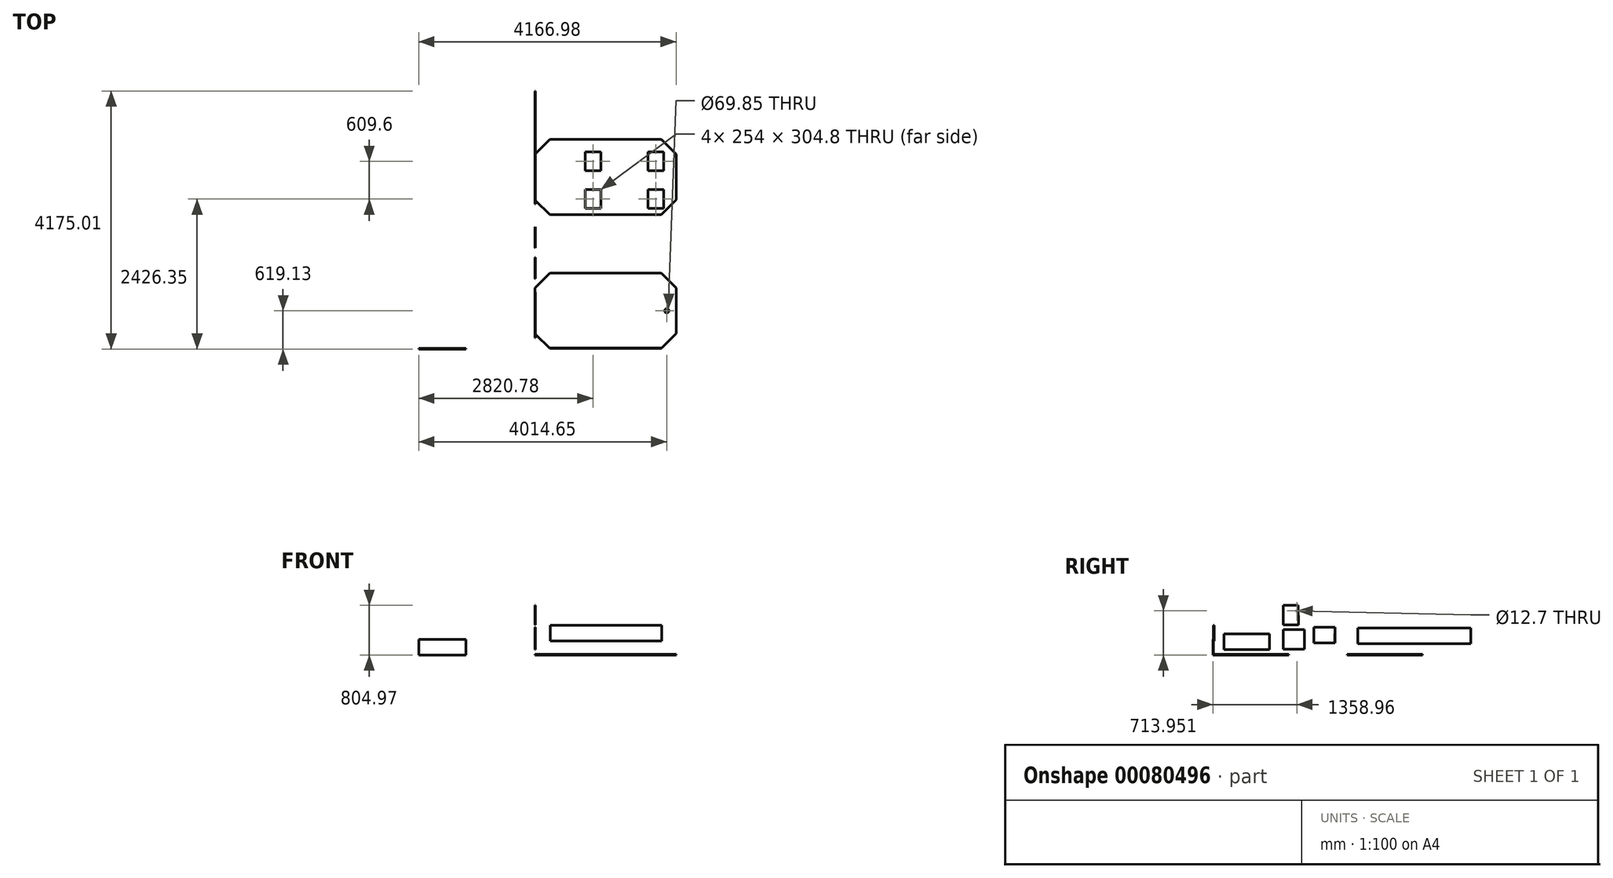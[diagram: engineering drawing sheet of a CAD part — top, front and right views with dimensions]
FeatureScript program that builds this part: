
annotation { "Feature Type Name" : "Feature", "Feature Type Description" : "" }
export const myFeature = defineFeature(function(context is Context, id is Id, definition is map)
    precondition{}
    {
        {
            var Q0;
            Q0=qCreatedBy(makeId("Top.planeOp"),FACE);
            var sketch = newSketch(context, id + "F0", { "sketchPlane" : qUnion([Q0])});
            skLineSegment(sketch, "E0.bottom", {"start": v(0, 0) * mm, "end": v(2438.4, 0) * mm});
            skLineSegment(sketch, "E0.top", {"start": v(0, 1219.2) * mm, "end": v(2438.4, 1219.2) * mm});
            skLineSegment(sketch, "E0.left", {"start": v(0, 0) * mm, "end": v(0, 1219.2) * mm});
            skLineSegment(sketch, "E0.right", {"start": v(2438.4, 0) * mm, "end": v(2438.4, 1219.2) * mm});
            skSolve(sketch);
        }
        {
            var Q0;
            Q0=makeQuery(id+"F0.imprint","IMPRINT",FACE,{"disambiguationData":[TD([[makeQuery(id+"F0.imprint","IMPRINT",EDGE,{"derivedFrom":sQuery(id+"F0.wireOp",EDGE,"E0.bottom")}),1.0]])]});
            extrude(context, id + "F1", {"entities" : qUnion([Q0]), "depth" : 9.52 * mm});
        }
        {
            var Q0;
            Q0=makeQuery(id+"F1.opExtrude","CAP_FACE",FACE,{"disambiguationData":[OSD([sQuery(id+"F0.wireOp",EDGE,"E0.bottom"),sQuery(id+"F0.wireOp",EDGE,"E0.top"),sQuery(id+"F0.wireOp",EDGE,"E0.left"),sQuery(id+"F0.wireOp",EDGE,"E0.right")])],"isStart":false});
            var sketch = newSketch(context, id + "F2", { "sketchPlane" : qUnion([Q0])});
            skLineSegment(sketch, "E1", {"start": v(0, 977.9) * mm, "end": v(241.3, 1219.2) * mm});
            skLineSegment(sketch, "E2", {"start": v(241.3, 1219.2) * mm, "end": v(0, 1219.2) * mm});
            skLineSegment(sketch, "E3", {"start": v(0, 1219.2) * mm, "end": v(0, 977.9) * mm});
            skLineSegment(sketch, "E4", {"start": v(0, 241.3) * mm, "end": v(241.3, 0) * mm});
            skLineSegment(sketch, "E5", {"start": v(241.3, 0) * mm, "end": v(0, 0) * mm});
            skLineSegment(sketch, "E6", {"start": v(0, 0) * mm, "end": v(0, 241.3) * mm});
            skSolve(sketch);
        }
        {
            var Q0;
            Q0=makeQuery(id+"F2.imprint","IMPRINT",FACE,{"disambiguationData":[TD([[makeQuery(id+"F2.imprint","IMPRINT",EDGE,{"derivedFrom":sQuery(id+"F2.wireOp",EDGE,"E1")}),1.0]])]});
            var Q1;
            Q1=makeQuery(id+"F2.imprint","IMPRINT",FACE,{"disambiguationData":[TD([[makeQuery(id+"F2.imprint","IMPRINT",EDGE,{"derivedFrom":sQuery(id+"F2.wireOp",EDGE,"E4")}),-1.0]])]});
            extrude(context, id + "F3", {"entities" : qUnion([Q0, Q1]), "operationType" : NewBodyOperationType.REMOVE, "oppositeDirection" : true, "depth" : 25.4 * mm});
        }
        {
            var Q0;
            Q0=makeQuery(id+"F1.opExtrude","CAP_FACE",FACE,{"disambiguationData":[OSD([sQuery(id+"F0.wireOp",EDGE,"E0.bottom"),sQuery(id+"F0.wireOp",EDGE,"E0.top"),sQuery(id+"F0.wireOp",EDGE,"E0.left"),sQuery(id+"F0.wireOp",EDGE,"E0.right")])],"isStart":false});
            var sketch = newSketch(context, id + "F4", { "sketchPlane" : qUnion([Q0])});
            skLineSegment(sketch, "E7.bottom", {"start": v(2438.4, 1219.2) * mm, "end": v(2044.7, 1219.2) * mm});
            skLineSegment(sketch, "E7.top", {"start": v(2438.4, 0) * mm, "end": v(2044.7, 0) * mm});
            skLineSegment(sketch, "E7.left", {"start": v(2438.4, 1219.2) * mm, "end": v(2438.4, 0) * mm});
            skLineSegment(sketch, "E8", {"start": v(2044.7, 1219.2) * mm, "end": v(2286, 977.9) * mm});
            skLineSegment(sketch, "E9", {"start": v(2286, 977.9) * mm, "end": v(2286, 241.3) * mm});
            skLineSegment(sketch, "E10", {"start": v(2286, 241.3) * mm, "end": v(2044.7, 0) * mm});
            skSolve(sketch);
        }
        {
            var Q0;
            Q0=makeQuery(id+"F4.imprint","IMPRINT",FACE,{"disambiguationData":[TD([[makeQuery(id+"F4.imprint","IMPRINT",EDGE,{"derivedFrom":sQuery(id+"F4.wireOp",EDGE,"E7.bottom")}),-1.0]])]});
            extrude(context, id + "F5", {"entities" : qUnion([Q0]), "operationType" : NewBodyOperationType.REMOVE, "oppositeDirection" : true, "depth" : 25.4 * mm});
        }
        {
            var Q0;
            Q0=qCreatedBy(makeId("Right.planeOp"),FACE);
            var sketch = newSketch(context, id + "F6", { "sketchPlane" : qUnion([Q0])});
            skLineSegment(sketch, "E11.bottom", {"start": v(172.56, 90.85) * mm, "end": v(909.16, 90.85) * mm});
            skLineSegment(sketch, "E11.top", {"start": v(172.56, 344.85) * mm, "end": v(909.16, 344.85) * mm});
            skLineSegment(sketch, "E11.left", {"start": v(172.56, 90.85) * mm, "end": v(172.56, 344.85) * mm});
            skLineSegment(sketch, "E11.right", {"start": v(909.16, 90.85) * mm, "end": v(909.16, 344.85) * mm});
            skSolve(sketch);
        }
        {
            var Q0;
            Q0=makeQuery(id+"F6.imprint","IMPRINT",FACE,{"disambiguationData":[TD([[makeQuery(id+"F6.imprint","IMPRINT",EDGE,{"derivedFrom":sQuery(id+"F6.wireOp",EDGE,"E11.bottom")}),1.0]])]});
            extrude(context, id + "F7", {"entities" : qUnion([Q0]), "depth" : 9.52 * mm});
        }
        {
            var Q0;
            Q0=qCreatedBy(makeId("Front.planeOp"),FACE);
            var sketch = newSketch(context, id + "F8", { "sketchPlane" : qUnion([Q0])});
            skLineSegment(sketch, "E12.top", {"start": v(2054.27, 480.87) * mm, "end": v(250.87, 480.87) * mm});
            skLineSegment(sketch, "E12.left", {"start": v(2054.27, 226.87) * mm, "end": v(2054.27, 480.87) * mm});
            skLineSegment(sketch, "E12.right", {"start": v(250.87, 226.87) * mm, "end": v(250.87, 480.87) * mm});
            skLineSegment(sketch, "E13", {"start": v(250.87, 226.87) * mm, "end": v(2054.27, 226.87) * mm});
            skSolve(sketch);
        }
        {
            var Q0;
            Q0=makeQuery(id+"F8.imprint","IMPRINT",FACE,{"disambiguationData":[TD([[makeQuery(id+"F8.imprint","IMPRINT",EDGE,{"derivedFrom":sQuery(id+"F8.wireOp",EDGE,"E12.bottom")}),-1.0]])]});
            var Q1;
            Q1=makeQuery(id+"F8.imprint","IMPRINT",FACE,{"disambiguationData":[TD([[makeQuery(id+"F8.imprint","IMPRINT",EDGE,{"derivedFrom":sQuery(id+"F8.wireOp",EDGE,"E12.top")}),1.0]])]});
            extrude(context, id + "F9", {"entities" : qUnion([Q0, Q1]), "oppositeDirection" : true, "depth" : 9.52 * mm});
        }
        {
            var Q0;
            Q0=qCreatedBy(makeId("Right.planeOp"),FACE);
            var sketch = newSketch(context, id + "F10", { "sketchPlane" : qUnion([Q0])});
            skLineSegment(sketch, "E14.bottom", {"start": v(28.65, 498.38) * mm, "end": v(765.25, 498.38) * mm});
            skLineSegment(sketch, "E14.top", {"start": v(28.65, 815.88) * mm, "end": v(765.25, 815.88) * mm});
            skLineSegment(sketch, "E14.left", {"start": v(28.65, 498.38) * mm, "end": v(28.65, 815.88) * mm});
            skLineSegment(sketch, "E14.right", {"start": v(765.25, 498.38) * mm, "end": v(765.25, 815.88) * mm});
            skSolve(sketch);
        }
        {
            var Q0;
            Q0=makeQuery(id+"F10.imprint","IMPRINT",FACE,{"disambiguationData":[TD([[makeQuery(id+"F10.imprint","IMPRINT",EDGE,{"derivedFrom":sQuery(id+"F10.wireOp",EDGE,"E14.bottom")}),1.0]])]});
            extrude(context, id + "F11", {"entities" : qUnion([Q0]), "depth" : 9.52 * mm});
        }
        {
            var Q0;
            Q0=qCreatedBy(makeId("Right.planeOp"),FACE);
            var sketch = newSketch(context, id + "F12", { "sketchPlane" : qUnion([Q0])});
            skLineSegment(sketch, "E15.bottom", {"start": v(1130.12, 487.47) * mm, "end": v(1384.12, 487.47) * mm});
            skLineSegment(sketch, "E15.top", {"start": v(1130.12, 804.97) * mm, "end": v(1384.12, 804.97) * mm});
            skLineSegment(sketch, "E15.left", {"start": v(1130.12, 487.47) * mm, "end": v(1130.12, 804.97) * mm});
            skLineSegment(sketch, "E15.right", {"start": v(1384.12, 487.47) * mm, "end": v(1384.12, 804.97) * mm});
            skSolve(sketch);
        }
        {
            var Q0;
            Q0=makeQuery(id+"F12.imprint","IMPRINT",FACE,{"disambiguationData":[TD([[makeQuery(id+"F12.imprint","IMPRINT",EDGE,{"derivedFrom":sQuery(id+"F12.wireOp",EDGE,"E15.bottom")}),1.0]])]});
            extrude(context, id + "F13", {"entities" : qUnion([Q0]), "depth" : 9.52 * mm});
        }
        {
            var Q0;
            Q0=makeQuery(id+"F13.opExtrude","SWEPT_FACE",FACE,{"disambiguationData":[OSD([sQuery(id+"F12.wireOp",EDGE,"E15.top")])]});
            var sketch = newSketch(context, id + "F14", { "sketchPlane" : qUnion([Q0])});
            skLineSegment(sketch, "E16", {"start": v(9.53, 1130.12) * mm, "end": v(0, 1139.64) * mm});
            skLineSegment(sketch, "E17", {"start": v(0, 1139.64) * mm, "end": v(0, 1130.12) * mm});
            skLineSegment(sketch, "E18", {"start": v(0, 1130.12) * mm, "end": v(9.52, 1130.12) * mm});
            skSolve(sketch);
        }
        {
            var Q0;
            Q0=makeQuery(id+"F14.imprint","IMPRINT",FACE,{"disambiguationData":[TD([[makeQuery(id+"F14.imprint","IMPRINT",EDGE,{"derivedFrom":sQuery(id+"F14.wireOp",EDGE,"i4C3c2Mx-m0kE-4Q8j-UAPY-lbmBrqHYXmZ3")}),-1.0]])]});
            var Q1;
            Q1=makeQuery(id+"F14.imprint","IMPRINT",FACE,{"disambiguationData":[TD([[makeQuery(id+"F14.imprint","IMPRINT",EDGE,{"derivedFrom":sQuery(id+"F14.wireOp",EDGE,"E16")}),1.0]])]});
            extrude(context, id + "F15", {"entities" : qUnion([Q0, Q1]), "operationType" : NewBodyOperationType.REMOVE, "oppositeDirection" : true, "depth" : 317.5 * mm});
        }
        {
            var Q0;
            Q0=makeQuery(id+"F13.opExtrude","SWEPT_EDGE",EDGE,{"disambiguationData":[OSD([sQuery(id+"F12.wireOp",EDGE,"E15.bottom"),sQuery(id+"F12.wireOp",EDGE,"E15.right")])]});
            var Q1;
            Q1=makeQuery(id+"F13.opExtrude","CAP_EDGE",EDGE,{"disambiguationData":[OSD([sQuery(id+"F12.wireOp",EDGE,"E15.bottom")])],"isStart":false});
            cPlane(context, id + "F16", {"entities" : qUnion([Q0, Q1]), "cplaneType" : CPlaneType.LINE_ANGLE, "offset" : 152.4 * mm, "angle" : 358.3 * degree, "width" : 152.4 * mm, "height" : 152.4 * mm});
        }
        {
            var Q0;
            Q0=qCreatedBy(id+"F16.planeOp",FACE);
            var sketch = newSketch(context, id + "F17", { "sketchPlane" : qUnion([Q0])});
            skLineSegment(sketch, "E19", {"start": v(9.54, -1393.98) * mm, "end": v(0, -1384.94) * mm});
            skLineSegment(sketch, "E20", {"start": v(0, -1384.94) * mm, "end": v(0, -1420.44) * mm});
            skLineSegment(sketch, "E21", {"start": v(0, -1420.44) * mm, "end": v(10.09, -1420.44) * mm});
            skLineSegment(sketch, "E22", {"start": v(10.09, -1420.44) * mm, "end": v(10.09, -1394.5) * mm});
            skLineSegment(sketch, "E23", {"start": v(9.54, -1393.98) * mm, "end": v(10.09, -1394.5) * mm});
            skSolve(sketch);
        }
        {
            var Q0;
            Q0=makeQuery(id+"F17.imprint","IMPRINT",FACE,{"disambiguationData":[TD([[makeQuery(id+"F17.imprint","IMPRINT",EDGE,{"derivedFrom":sQuery(id+"F17.wireOp",EDGE,"E19")}),1.0]])]});
            extrude(context, id + "F18", {"entities" : qUnion([Q0]), "operationType" : NewBodyOperationType.REMOVE, "oppositeDirection" : true, "depth" : 330.2 * mm});
        }
        {
            var Q0;
            Q0=makeQuery(id+"F13.opExtrude","CAP_FACE",FACE,{"disambiguationData":[OSD([sQuery(id+"F12.wireOp",EDGE,"E15.bottom"),sQuery(id+"F12.wireOp",EDGE,"E15.top"),sQuery(id+"F12.wireOp",EDGE,"E15.left"),sQuery(id+"F12.wireOp",EDGE,"E15.right")])],"isStart":false});
            var sketch = newSketch(context, id + "F19", { "sketchPlane" : qUnion([Q0])});
            skCircle(sketch, "E24", {"center": v(1349.43, 713.95) * mm, "radius": 6.35 * mm});
            skSolve(sketch);
        }
        {
            var Q0;
            Q0=makeQuery(id+"F19.imprint","IMPRINT",FACE,{"disambiguationData":[TD([[makeQuery(id+"F19.imprint","IMPRINT",EDGE,{"derivedFrom":sQuery(id+"F19.wireOp",EDGE,"E24")}),1.0]])]});
            extrude(context, id + "F20", {"entities" : qUnion([Q0]), "operationType" : NewBodyOperationType.REMOVE, "oppositeDirection" : true, "depth" : 25.4 * mm});
        }
        {
            var Q0;
            Q0=qCreatedBy(makeId("Right.planeOp"),FACE);
            var sketch = newSketch(context, id + "F21", { "sketchPlane" : qUnion([Q0])});
            skLineSegment(sketch, "E25.bottom", {"start": v(1131.07, 411.37) * mm, "end": v(1473.97, 411.37) * mm});
            skLineSegment(sketch, "E25.top", {"start": v(1131.07, 93.87) * mm, "end": v(1473.97, 93.87) * mm});
            skLineSegment(sketch, "E25.left", {"start": v(1131.07, 411.37) * mm, "end": v(1131.07, 93.87) * mm});
            skLineSegment(sketch, "E25.right", {"start": v(1473.97, 411.37) * mm, "end": v(1473.97, 93.87) * mm});
            skSolve(sketch);
        }
        {
            var Q0;
            Q0=qCreatedBy(makeId("Right.planeOp"),FACE);
            var sketch = newSketch(context, id + "F22", { "sketchPlane" : qUnion([Q0])});
            skLineSegment(sketch, "E26.bottom", {"start": v(1623.64, 450.22) * mm, "end": v(1966.54, 450.22) * mm});
            skLineSegment(sketch, "E26.top", {"start": v(1623.64, 196.22) * mm, "end": v(1966.54, 196.22) * mm});
            skLineSegment(sketch, "E26.left", {"start": v(1623.64, 450.22) * mm, "end": v(1623.64, 196.22) * mm});
            skLineSegment(sketch, "E26.right", {"start": v(1966.54, 450.22) * mm, "end": v(1966.54, 196.22) * mm});
            skSolve(sketch);
        }
        {
            var Q0;
            Q0=makeQuery(id+"F21.imprint","IMPRINT",FACE,{"disambiguationData":[TD([[makeQuery(id+"F21.imprint","IMPRINT",EDGE,{"derivedFrom":sQuery(id+"F21.wireOp",EDGE,"E25.bottom")}),-1.0]])]});
            extrude(context, id + "F23", {"entities" : qUnion([Q0]), "depth" : 9.52 * mm});
        }
        {
            var Q0;
            Q0=makeQuery(id+"F22.imprint","IMPRINT",FACE,{"disambiguationData":[TD([[makeQuery(id+"F22.imprint","IMPRINT",EDGE,{"derivedFrom":sQuery(id+"F22.wireOp",EDGE,"E26.bottom")}),-1.0]])]});
            extrude(context, id + "F24", {"entities" : qUnion([Q0]), "depth" : 9.52 * mm});
        }
        {
            var Q0;
            Q0=qCreatedBy(makeId("Top.planeOp"),FACE);
            var sketch = newSketch(context, id + "F25", { "sketchPlane" : qUnion([Q0])});
            skLineSegment(sketch, "E27.bottom", {"start": v(0, 2162.82) * mm, "end": v(2286, 2162.82) * mm});
            skLineSegment(sketch, "E27.top", {"start": v(0, 3382.02) * mm, "end": v(2286, 3382.02) * mm});
            skLineSegment(sketch, "E27.left", {"start": v(0, 2162.82) * mm, "end": v(0, 3382.02) * mm});
            skLineSegment(sketch, "E27.right", {"start": v(2286, 2162.82) * mm, "end": v(2286, 3382.02) * mm});
            skSolve(sketch);
        }
        {
            var Q0;
            Q0=makeQuery(id+"F25.imprint","IMPRINT",FACE,{"disambiguationData":[TD([[makeQuery(id+"F25.imprint","IMPRINT",EDGE,{"derivedFrom":sQuery(id+"F25.wireOp",EDGE,"E27.bottom")}),1.0]])]});
            extrude(context, id + "F26", {"entities" : qUnion([Q0]), "depth" : 9.52 * mm});
        }
        {
            var Q0;
            Q0=makeQuery(id+"F26.opExtrude","CAP_FACE",FACE,{"disambiguationData":[OSD([sQuery(id+"F25.wireOp",EDGE,"E27.bottom"),sQuery(id+"F25.wireOp",EDGE,"E27.top"),sQuery(id+"F25.wireOp",EDGE,"E27.left"),sQuery(id+"F25.wireOp",EDGE,"E27.right")])],"isStart":false});
            var sketch = newSketch(context, id + "F27", { "sketchPlane" : qUnion([Q0])});
            skLineSegment(sketch, "E28.bottom", {"start": v(0, 3382.02) * mm, "end": v(241.3, 3382.02) * mm});
            skLineSegment(sketch, "E28.left", {"start": v(0, 3382.02) * mm, "end": v(0, 3140.72) * mm});
            skLineSegment(sketch, "E29.bottom", {"start": v(0, 2162.82) * mm, "end": v(241.3, 2162.82) * mm});
            skLineSegment(sketch, "E29.left", {"start": v(0, 2162.82) * mm, "end": v(0, 2404.12) * mm});
            skLineSegment(sketch, "E30.bottom", {"start": v(2286, 3382.02) * mm, "end": v(2044.7, 3382.02) * mm});
            skLineSegment(sketch, "E31.bottom", {"start": v(2286, 2162.82) * mm, "end": v(2044.7, 2162.82) * mm});
            skLineSegment(sketch, "E32", {"start": v(0, 3140.72) * mm, "end": v(241.3, 3382.02) * mm});
            skLineSegment(sketch, "E33", {"start": v(0, 2404.12) * mm, "end": v(241.3, 2162.82) * mm});
            skLineSegment(sketch, "E34", {"start": v(2286, 3382.02) * mm, "end": v(2286, 3140.72) * mm});
            skLineSegment(sketch, "E35", {"start": v(2286, 3140.72) * mm, "end": v(2044.7, 3382.02) * mm});
            skLineSegment(sketch, "E36", {"start": v(2286, 2162.82) * mm, "end": v(2286, 2404.12) * mm});
            skLineSegment(sketch, "E37", {"start": v(2286, 2404.12) * mm, "end": v(2044.7, 2162.82) * mm});
            skSolve(sketch);
        }
        {
            var Q0;
            Q0=makeQuery(id+"F27.imprint","IMPRINT",FACE,{"disambiguationData":[TD([[makeQuery(id+"F27.imprint","IMPRINT",EDGE,{"derivedFrom":sQuery(id+"F27.wireOp",EDGE,"E28.bottom")}),-1.0]])]});
            var Q1;
            Q1=makeQuery(id+"F27.imprint","IMPRINT",FACE,{"disambiguationData":[TD([[makeQuery(id+"F27.imprint","IMPRINT",EDGE,{"derivedFrom":sQuery(id+"F27.wireOp",EDGE,"E29.bottom")}),1.0]])]});
            var Q2;
            Q2=makeQuery(id+"F27.imprint","IMPRINT",FACE,{"disambiguationData":[TD([[makeQuery(id+"F27.imprint","IMPRINT",EDGE,{"derivedFrom":sQuery(id+"F27.wireOp",EDGE,"E30.bottom")}),-1.0]])]});
            var Q3;
            Q3=makeQuery(id+"F27.imprint","IMPRINT",FACE,{"disambiguationData":[TD([[makeQuery(id+"F27.imprint","IMPRINT",EDGE,{"derivedFrom":sQuery(id+"F27.wireOp",EDGE,"E31.bottom")}),1.0]])]});
            extrude(context, id + "F28", {"entities" : qUnion([Q0, Q1, Q2, Q3]), "operationType" : NewBodyOperationType.REMOVE, "oppositeDirection" : true, "depth" : 25.4 * mm});
        }
        {
            var Q0;
            Q0=makeQuery(id+"F1.opExtrude","CAP_EDGE",EDGE,{"disambiguationData":[OSD([sQuery(id+"F0.wireOp",EDGE,"E0.left")])],"isStart":false});
            cPlane(context, id + "F29", {"entities" : qUnion([Q0]), "cplaneType" : CPlaneType.LINE_ANGLE, "offset" : 152.4 * mm, "angle" : 358.8 * degree, "width" : 152.4 * mm, "height" : 152.4 * mm});
        }
        {
            var Q0;
            Q0=qCreatedBy(id+"F29.planeOp",FACE);
            var sketch = newSketch(context, id + "F30", { "sketchPlane" : qUnion([Q0])});
            skLineSegment(sketch, "E38.bottom", {"start": v(0, 211.48) * mm, "end": v(-33.38, 211.48) * mm});
            skLineSegment(sketch, "E38.top", {"start": v(0, 1019.73) * mm, "end": v(-33.38, 1019.73) * mm});
            skLineSegment(sketch, "E38.left", {"start": v(0, 211.48) * mm, "end": v(0, 1019.73) * mm});
            skLineSegment(sketch, "E38.right", {"start": v(-33.38, 211.48) * mm, "end": v(-33.38, 1019.73) * mm});
            skSolve(sketch);
        }
        {
            var Q0;
            Q0=makeQuery(id+"F30.imprint","IMPRINT",FACE,{"disambiguationData":[TD([[makeQuery(id+"F30.imprint","IMPRINT",EDGE,{"derivedFrom":sQuery(id+"F30.wireOp",EDGE,"E38.bottom")}),-1.0]])]});
            extrude(context, id + "F31", {"entities" : qUnion([Q0]), "operationType" : NewBodyOperationType.REMOVE, "oppositeDirection" : true, "depth" : 25.4 * mm});
        }
        {
            var Q0;
            Q0=qCreatedBy(makeId("Right.planeOp"),FACE);
            var sketch = newSketch(context, id + "F32", { "sketchPlane" : qUnion([Q0])});
            skLineSegment(sketch, "E39.bottom", {"start": v(2336.68, 182.8) * mm, "end": v(4165.48, 182.8) * mm});
            skLineSegment(sketch, "E39.top", {"start": v(2336.68, 436.8) * mm, "end": v(4165.48, 436.8) * mm});
            skLineSegment(sketch, "E39.left", {"start": v(2336.68, 182.8) * mm, "end": v(2336.68, 436.8) * mm});
            skLineSegment(sketch, "E39.right", {"start": v(4165.48, 182.8) * mm, "end": v(4165.48, 436.8) * mm});
            skSolve(sketch);
        }
        {
            var Q0;
            Q0=makeQuery(id+"F32.imprint","IMPRINT",FACE,{"disambiguationData":[TD([[makeQuery(id+"F32.imprint","IMPRINT",EDGE,{"derivedFrom":sQuery(id+"F32.wireOp",EDGE,"E39.bottom")}),1.0]])]});
            extrude(context, id + "F33", {"entities" : qUnion([Q0]), "depth" : 9.52 * mm});
        }
        {
            var Q0;
            Q0=qCreatedBy(makeId("Front.planeOp"),FACE);
            var sketch = newSketch(context, id + "F34", { "sketchPlane" : qUnion([Q0])});
            skLineSegment(sketch, "E40.bottom", {"start": v(-1118.98, 0) * mm, "end": v(-1880.98, 0) * mm});
            skLineSegment(sketch, "E40.top", {"start": v(-1118.98, 254) * mm, "end": v(-1880.98, 254) * mm});
            skLineSegment(sketch, "E40.left", {"start": v(-1118.98, 0) * mm, "end": v(-1118.98, 254) * mm});
            skLineSegment(sketch, "E40.right", {"start": v(-1880.98, 0) * mm, "end": v(-1880.98, 254) * mm});
            skSolve(sketch);
        }
        {
            var Q0;
            Q0=makeQuery(id+"F34.imprint","IMPRINT",FACE,{"disambiguationData":[TD([[makeQuery(id+"F34.imprint","IMPRINT",EDGE,{"derivedFrom":sQuery(id+"F34.wireOp",EDGE,"E40.bottom")}),-1.0]])]});
            extrude(context, id + "F35", {"entities" : qUnion([Q0]), "depth" : 9.52 * mm});
        }
        {
            var Q0;
            Q0=makeQuery(id+"F24.opExtrude","SWEPT_FACE",FACE,{"disambiguationData":[OSD([sQuery(id+"F22.wireOp",EDGE,"E26.bottom")])]});
            var sketch = newSketch(context, id + "F36", { "sketchPlane" : qUnion([Q0])});
            skLineSegment(sketch, "E41", {"start": v(9.53, 1966.54) * mm, "end": v(0, 1957.02) * mm});
            skLineSegment(sketch, "E42", {"start": v(0, 1957.02) * mm, "end": v(0, 1966.54) * mm});
            skLineSegment(sketch, "E43", {"start": v(0, 1966.54) * mm, "end": v(9.52, 1966.54) * mm});
            skLineSegment(sketch, "E44", {"start": v(0, 1623.64) * mm, "end": v(0, 1633.17) * mm});
            skLineSegment(sketch, "E45", {"start": v(0, 1633.17) * mm, "end": v(9.52, 1623.64) * mm});
            skLineSegment(sketch, "E46", {"start": v(9.52, 1623.64) * mm, "end": v(0, 1623.64) * mm});
            skSolve(sketch);
        }
        {
            var Q0;
            Q0=makeQuery(id+"F36.imprint","IMPRINT",FACE,{"disambiguationData":[TD([[makeQuery(id+"F36.imprint","IMPRINT",EDGE,{"derivedFrom":sQuery(id+"F36.wireOp",EDGE,"E41")}),-1.0]])]});
            var Q1;
            Q1=makeQuery(id+"F36.imprint","IMPRINT",FACE,{"disambiguationData":[TD([[makeQuery(id+"F36.imprint","IMPRINT",EDGE,{"derivedFrom":sQuery(id+"F36.wireOp",EDGE,"E44")}),-1.0]])]});
            extrude(context, id + "F37", {"entities" : qUnion([Q0, Q1]), "operationType" : NewBodyOperationType.REMOVE, "oppositeDirection" : true, "depth" : 254 * mm});
        }
        {
            var Q0;
            Q0=makeQuery(id+"F26.opExtrude","CAP_FACE",FACE,{"disambiguationData":[OSD([sQuery(id+"F25.wireOp",EDGE,"E27.bottom"),sQuery(id+"F25.wireOp",EDGE,"E27.top"),sQuery(id+"F25.wireOp",EDGE,"E27.left"),sQuery(id+"F25.wireOp",EDGE,"E27.right")])],"isStart":false});
            var sketch = newSketch(context, id + "F38", { "sketchPlane" : qUnion([Q0])});
            skLineSegment(sketch, "E47.bottom", {"start": v(812.8, 3178.82) * mm, "end": v(1066.8, 3178.82) * mm});
            skLineSegment(sketch, "E47.top", {"start": v(812.8, 2874.02) * mm, "end": v(1066.8, 2874.02) * mm});
            skLineSegment(sketch, "E47.left", {"start": v(812.8, 3178.82) * mm, "end": v(812.8, 2874.02) * mm});
            skLineSegment(sketch, "E47.right", {"start": v(1066.8, 3178.82) * mm, "end": v(1066.8, 2874.02) * mm});
            skLineSegment(sketch, "E48.bottom", {"start": v(812.8, 2569.22) * mm, "end": v(1066.8, 2569.22) * mm});
            skLineSegment(sketch, "E48.top", {"start": v(812.8, 2264.42) * mm, "end": v(1066.8, 2264.42) * mm});
            skLineSegment(sketch, "E48.left", {"start": v(812.8, 2569.22) * mm, "end": v(812.8, 2264.42) * mm});
            skLineSegment(sketch, "E48.right", {"start": v(1066.8, 2569.22) * mm, "end": v(1066.8, 2264.42) * mm});
            skLineSegment(sketch, "E49.bottom", {"start": v(1828.8, 2874.02) * mm, "end": v(2082.8, 2874.02) * mm});
            skLineSegment(sketch, "E49.top", {"start": v(1828.8, 3178.82) * mm, "end": v(2082.8, 3178.82) * mm});
            skLineSegment(sketch, "E49.left", {"start": v(1828.8, 2874.02) * mm, "end": v(1828.8, 3178.82) * mm});
            skLineSegment(sketch, "E49.right", {"start": v(2082.8, 2874.02) * mm, "end": v(2082.8, 3178.82) * mm});
            skLineSegment(sketch, "E50.bottom", {"start": v(1828.8, 2569.22) * mm, "end": v(2082.8, 2569.22) * mm});
            skLineSegment(sketch, "E50.top", {"start": v(1828.8, 2264.42) * mm, "end": v(2082.8, 2264.42) * mm});
            skLineSegment(sketch, "E50.left", {"start": v(1828.8, 2569.22) * mm, "end": v(1828.8, 2264.42) * mm});
            skLineSegment(sketch, "E50.right", {"start": v(2082.8, 2569.22) * mm, "end": v(2082.8, 2264.42) * mm});
            skSolve(sketch);
        }
        {
            var Q0;
            Q0=makeQuery(id+"F38.imprint","IMPRINT",FACE,{"disambiguationData":[TD([[makeQuery(id+"F38.imprint","IMPRINT",EDGE,{"derivedFrom":sQuery(id+"F38.wireOp",EDGE,"E47.bottom")}),-1.0]])]});
            var Q1;
            Q1=makeQuery(id+"F38.imprint","IMPRINT",FACE,{"disambiguationData":[TD([[makeQuery(id+"F38.imprint","IMPRINT",EDGE,{"derivedFrom":sQuery(id+"F38.wireOp",EDGE,"E48.bottom")}),-1.0]])]});
            var Q2;
            Q2=makeQuery(id+"F38.imprint","IMPRINT",FACE,{"disambiguationData":[TD([[makeQuery(id+"F38.imprint","IMPRINT",EDGE,{"derivedFrom":sQuery(id+"F38.wireOp",EDGE,"E49.bottom")}),1.0]])]});
            var Q3;
            Q3=makeQuery(id+"F38.imprint","IMPRINT",FACE,{"disambiguationData":[TD([[makeQuery(id+"F38.imprint","IMPRINT",EDGE,{"derivedFrom":sQuery(id+"F38.wireOp",EDGE,"E50.bottom")}),-1.0]])]});
            extrude(context, id + "F39", {"entities" : qUnion([Q0, Q1, Q2, Q3]), "operationType" : NewBodyOperationType.REMOVE, "oppositeDirection" : true, "depth" : 101.6 * mm});
        }
        {
            var Q0;
            Q0=qCreatedBy(id+"F29.planeOp",FACE);
            var sketch = newSketch(context, id + "F40", { "sketchPlane" : qUnion([Q0])});
            skCircle(sketch, "E51", {"center": v(2133.3, 609.6) * mm, "radius": 34.93 * mm});
            skSolve(sketch);
        }
        {
            var Q0;
            Q0=makeQuery(id+"F40.imprint","IMPRINT",FACE,{"disambiguationData":[TD([[makeQuery(id+"F40.imprint","IMPRINT",EDGE,{"derivedFrom":sQuery(id+"F40.wireOp",EDGE,"E51")}),1.0]])]});
            extrude(context, id + "F41", {"entities" : qUnion([Q0]), "operationType" : NewBodyOperationType.REMOVE, "oppositeDirection" : true, "depth" : 127 * mm});
        }
        {
            var Q0;
            Q0=makeQuery(id+"F11.opExtrude","SWEPT_BODY",BODY,{"disambiguationData":[OSD([sQuery(id+"F10.wireOp",EDGE,"E14.bottom"),sQuery(id+"F10.wireOp",EDGE,"E14.top"),sQuery(id+"F10.wireOp",EDGE,"E14.left"),sQuery(id+"F10.wireOp",EDGE,"E14.right")])]});
            deleteBodies(context, id + "F42", {"entities" : qUnion([Q0])});
        }
    });
